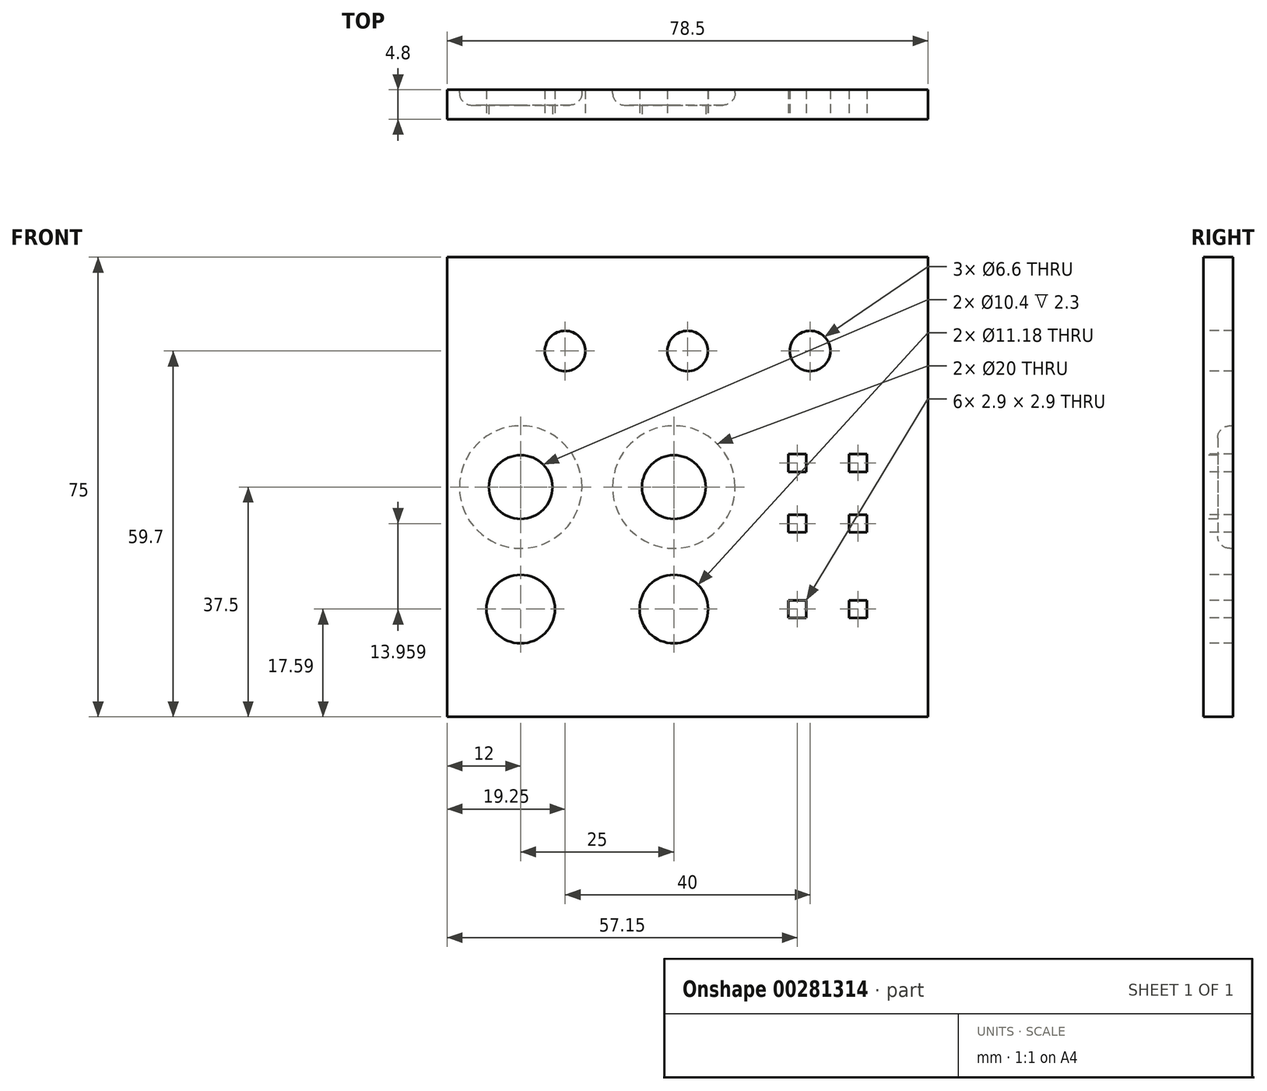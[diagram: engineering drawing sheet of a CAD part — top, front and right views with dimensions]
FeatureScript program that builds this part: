
annotation { "Feature Type Name" : "Feature", "Feature Type Description" : "" }
export const myFeature = defineFeature(function(context is Context, id is Id, definition is map)
    precondition{}
    {
        {
            var Q0;
            Q0=qCreatedBy(makeId("Front.planeOp"),FACE);
            var sketch = newSketch(context, id + "F0", { "sketchPlane" : qUnion([Q0])});
            skLineSegment(sketch, "E0.bottom", {"start": v(39.25, -37.5) * mm, "end": v(-39.25, -37.5) * mm});
            skLineSegment(sketch, "E0.top", {"start": v(39.25, 37.5) * mm, "end": v(-39.25, 37.5) * mm});
            skLineSegment(sketch, "E0.left", {"start": v(39.25, -37.5) * mm, "end": v(39.25, 37.5) * mm});
            skLineSegment(sketch, "E0.right", {"start": v(-39.25, -37.5) * mm, "end": v(-39.25, 37.5) * mm});
            skPoint(sketch, "E0.middle", {"position": v(0, 0) * mm});
            skSolve(sketch);
        }
        {
            var Q0;
            Q0=qSketchRegion(id+"F0",true);
            extrude(context, id + "F1", {"entities" : qUnion([Q0]), "depth" : 4.8 * mm});
        }
        {
            var Q0;
            Q0=makeQuery(id+"F1.opExtrude","CAP_FACE",FACE,{"disambiguationData":[OSD([sQuery(id+"F0.wireOp",EDGE,"E0.bottom"),sQuery(id+"F0.wireOp",EDGE,"E0.top"),sQuery(id+"F0.wireOp",EDGE,"E0.left"),sQuery(id+"F0.wireOp",EDGE,"E0.right")])],"isStart":false});
            var sketch = newSketch(context, id + "F2", { "sketchPlane" : qUnion([Q0])});
            skCircle(sketch, "E1", {"center": v(-27.25, 0) * mm, "radius": 5.2 * mm});
            skCircle(sketch, "E2", {"center": v(-27.25, -19.91) * mm, "radius": 5.6 * mm});
            skCircle(sketch, "E3", {"center": v(-2.25, -19.91) * mm, "radius": 5.6 * mm});
            skCircle(sketch, "E4", {"center": v(-2.25, 0) * mm, "radius": 5.2 * mm});
            skCircle(sketch, "E5", {"center": v(0, 22.2) * mm, "radius": 3.3 * mm});
            skCircle(sketch, "E6", {"center": v(-20, 22.2) * mm, "radius": 3.3 * mm});
            skCircle(sketch, "E7", {"center": v(20, 22.2) * mm, "radius": 3.3 * mm});
            skLineSegment(sketch, "E8.bottom", {"start": v(19.35, 2.5) * mm, "end": v(16.45, 2.5) * mm});
            skLineSegment(sketch, "E8.top", {"start": v(19.35, 5.4) * mm, "end": v(16.45, 5.4) * mm});
            skLineSegment(sketch, "E8.left", {"start": v(19.35, 2.5) * mm, "end": v(19.35, 5.4) * mm});
            skLineSegment(sketch, "E8.right", {"start": v(16.45, 2.5) * mm, "end": v(16.45, 5.4) * mm});
            skPoint(sketch, "E8.middle", {"position": v(17.9, 3.95) * mm});
            skLineSegment(sketch, "E9.bottom", {"start": v(26.35, 5.4) * mm, "end": v(29.25, 5.4) * mm});
            skLineSegment(sketch, "E9.top", {"start": v(26.35, 2.5) * mm, "end": v(29.25, 2.5) * mm});
            skLineSegment(sketch, "E9.left", {"start": v(26.35, 5.4) * mm, "end": v(26.35, 2.5) * mm});
            skLineSegment(sketch, "E9.right", {"start": v(29.25, 5.4) * mm, "end": v(29.25, 2.5) * mm});
            skPoint(sketch, "E9.middle", {"position": v(27.8, 3.95) * mm});
            skLineSegment(sketch, "E10.bottom", {"start": v(19.35, -7.4) * mm, "end": v(16.45, -7.4) * mm});
            skLineSegment(sketch, "E10.top", {"start": v(19.35, -4.5) * mm, "end": v(16.45, -4.5) * mm});
            skLineSegment(sketch, "E10.left", {"start": v(19.35, -7.4) * mm, "end": v(19.35, -4.5) * mm});
            skLineSegment(sketch, "E10.right", {"start": v(16.45, -7.4) * mm, "end": v(16.45, -4.5) * mm});
            skPoint(sketch, "E10.middle", {"position": v(17.9, -5.95) * mm});
            skLineSegment(sketch, "E11.bottom", {"start": v(29.25, -7.4) * mm, "end": v(26.35, -7.4) * mm});
            skLineSegment(sketch, "E11.top", {"start": v(29.25, -4.5) * mm, "end": v(26.35, -4.5) * mm});
            skLineSegment(sketch, "E11.left", {"start": v(29.25, -7.4) * mm, "end": v(29.25, -4.5) * mm});
            skLineSegment(sketch, "E11.right", {"start": v(26.35, -7.4) * mm, "end": v(26.35, -4.5) * mm});
            skPoint(sketch, "E11.middle", {"position": v(27.8, -5.95) * mm});
            skLineSegment(sketch, "E12.bottom", {"start": v(19.35, -21.36) * mm, "end": v(16.45, -21.36) * mm});
            skLineSegment(sketch, "E12.top", {"start": v(19.35, -18.46) * mm, "end": v(16.45, -18.46) * mm});
            skLineSegment(sketch, "E12.left", {"start": v(19.35, -21.36) * mm, "end": v(19.35, -18.46) * mm});
            skLineSegment(sketch, "E12.right", {"start": v(16.45, -21.36) * mm, "end": v(16.45, -18.46) * mm});
            skPoint(sketch, "E12.middle", {"position": v(17.9, -19.9) * mm});
            skPoint(sketch, "E13.middle.positionSnap0", {"position": v(19.35, -19.9) * mm});
            skPoint(sketch, "E13.centerSnap0", {"position": v(19.35, -19.9) * mm});
            skLineSegment(sketch, "E14.bottom", {"start": v(26.35, -21.36) * mm, "end": v(29.25, -21.36) * mm});
            skLineSegment(sketch, "E14.top", {"start": v(26.35, -18.46) * mm, "end": v(29.25, -18.46) * mm});
            skLineSegment(sketch, "E14.left", {"start": v(26.35, -21.36) * mm, "end": v(26.35, -18.46) * mm});
            skLineSegment(sketch, "E14.right", {"start": v(29.25, -21.36) * mm, "end": v(29.25, -18.46) * mm});
            skPoint(sketch, "E14.middle", {"position": v(27.8, -19.9) * mm});
            skSolve(sketch);
        }
        {
            var Q0;
            Q0=qSketchRegion(id+"F2",true);
            extrude(context, id + "F3", {"entities" : qUnion([Q0]), "operationType" : NewBodyOperationType.REMOVE, "endBound" : BoundingType.THROUGH_ALL, "oppositeDirection" : true, "depth" : 25 * mm});
        }
        {
            var Q0;
            Q0=makeQuery(id+"F1.opExtrude","CAP_FACE",FACE,{"disambiguationData":[OSD([sQuery(id+"F0.wireOp",EDGE,"E0.bottom"),sQuery(id+"F0.wireOp",EDGE,"E0.top"),sQuery(id+"F0.wireOp",EDGE,"E0.left"),sQuery(id+"F0.wireOp",EDGE,"E0.right")])],"isStart":true});
            var sketch = newSketch(context, id + "F4", { "sketchPlane" : qUnion([Q0])});
            skCircle(sketch, "E15", {"center": v(2.25, 0) * mm, "radius": 10 * mm});
            skCircle(sketch, "E16", {"center": v(27.25, 0) * mm, "radius": 10 * mm});
            skSolve(sketch);
        }
        {
            var Q0;
            Q0 = qSketchRegion(id + "F4", true);
            extrude(context, id + "F5", {"entities" : qUnion([Q0]), "operationType" : NewBodyOperationType.REMOVE, "oppositeDirection" : true, "depth" : 2.5 * mm});
        }
        {
            var Q0;
            Q0=makeQuery(id+"F5.boolean.opBoolean","COPY",EDGE,{"derivedFrom":makeQuery(id+"F5.opExtrude","CAP_EDGE",EDGE,{"disambiguationData":[OSD([sQuery(id+"F4.wireOp",EDGE,"E15")])],"isStart":false})});
            var Q1;
            Q1=makeQuery(id+"F5.boolean.opBoolean","COPY",EDGE,{"derivedFrom":makeQuery(id+"F5.opExtrude","CAP_EDGE",EDGE,{"disambiguationData":[OSD([sQuery(id+"F4.wireOp",EDGE,"E16")])],"isStart":false})});
            fillet(context, id + "F6", {"entities" : qUnion([Q0, Q1]), "radius" : 2 * mm, "tangentPropagation" : true, "allowEdgeOverflow" : false});
        }
    });
